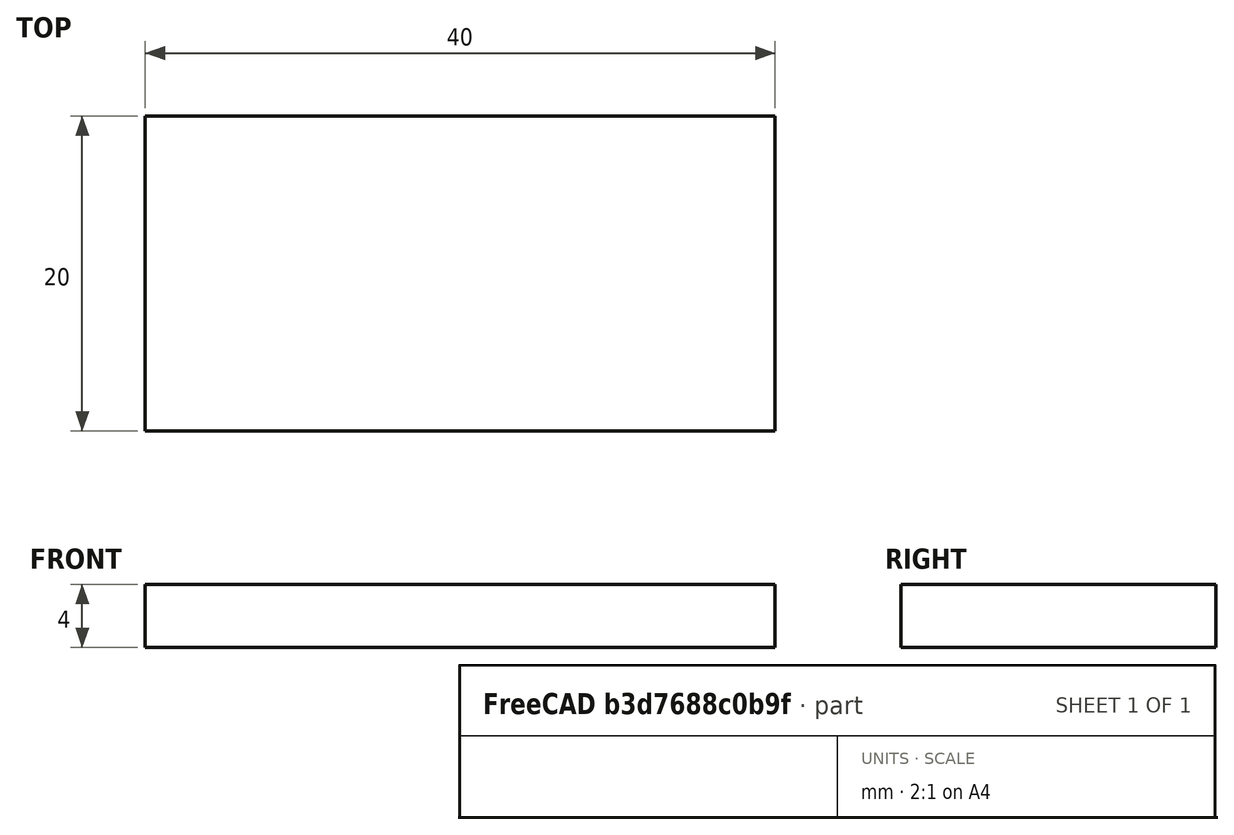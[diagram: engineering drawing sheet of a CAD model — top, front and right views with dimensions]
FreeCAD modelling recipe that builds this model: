
FCSTD DOCUMENT  (FreeCAD 0.20R29410 (Git))
Label: base
License: Creative Commons Attribution
LicenseURL: http://creativecommons.org/licenses/by/4.0/
objects: Sketcher::SketchObject×1, Part::Extrusion×1
note: 2 computed .brp shape members not serialized (recipe doc carries the construction recipe); baked Part::Feature solids carry a one-line shape summary decoded from their .brp

FEATURE [Sketcher::SketchObject] Sketch  label="plano_base"
  FullyConstrained = true
  sketch-geometry (4):
    g0: LineSegment StartX=0 StartY=0 StartZ=0 EndX=0 EndY=20 EndZ=0
    g1: LineSegment StartX=0 StartY=20 StartZ=0 EndX=40 EndY=20 EndZ=0
    g2: LineSegment StartX=40 StartY=20 StartZ=0 EndX=40 EndY=0 EndZ=0
    g3: LineSegment StartX=40 StartY=0 StartZ=0 EndX=0 EndY=0 EndZ=0
  constraints (11):
    c: Horizontal(g1)
    c: Horizontal(g3)
    c: Vertical(g0)
    c: Vertical(g2)
    c: Coincident(g1,g0)
    c: Coincident(g1,g2)
    c: Coincident(g3,g0)
    c: Coincident(g3,g2)
    c: Coincident(g0,g-1)
    c: DistanceX(g1,g1) = 40  'Width'
    c: DistanceY(g0,g0) = 20  'Height'
FEATURE [Part::Extrusion] Extrude  label="base_extruida"
  Base = -> Sketch
  Dir = (0,0,1)
  DirMode = 2
  FaceMakerClass = Part::FaceMakerBullseye
  LengthFwd = 4
  LengthRev = 0
  Solid = true
  Symmetric = false
